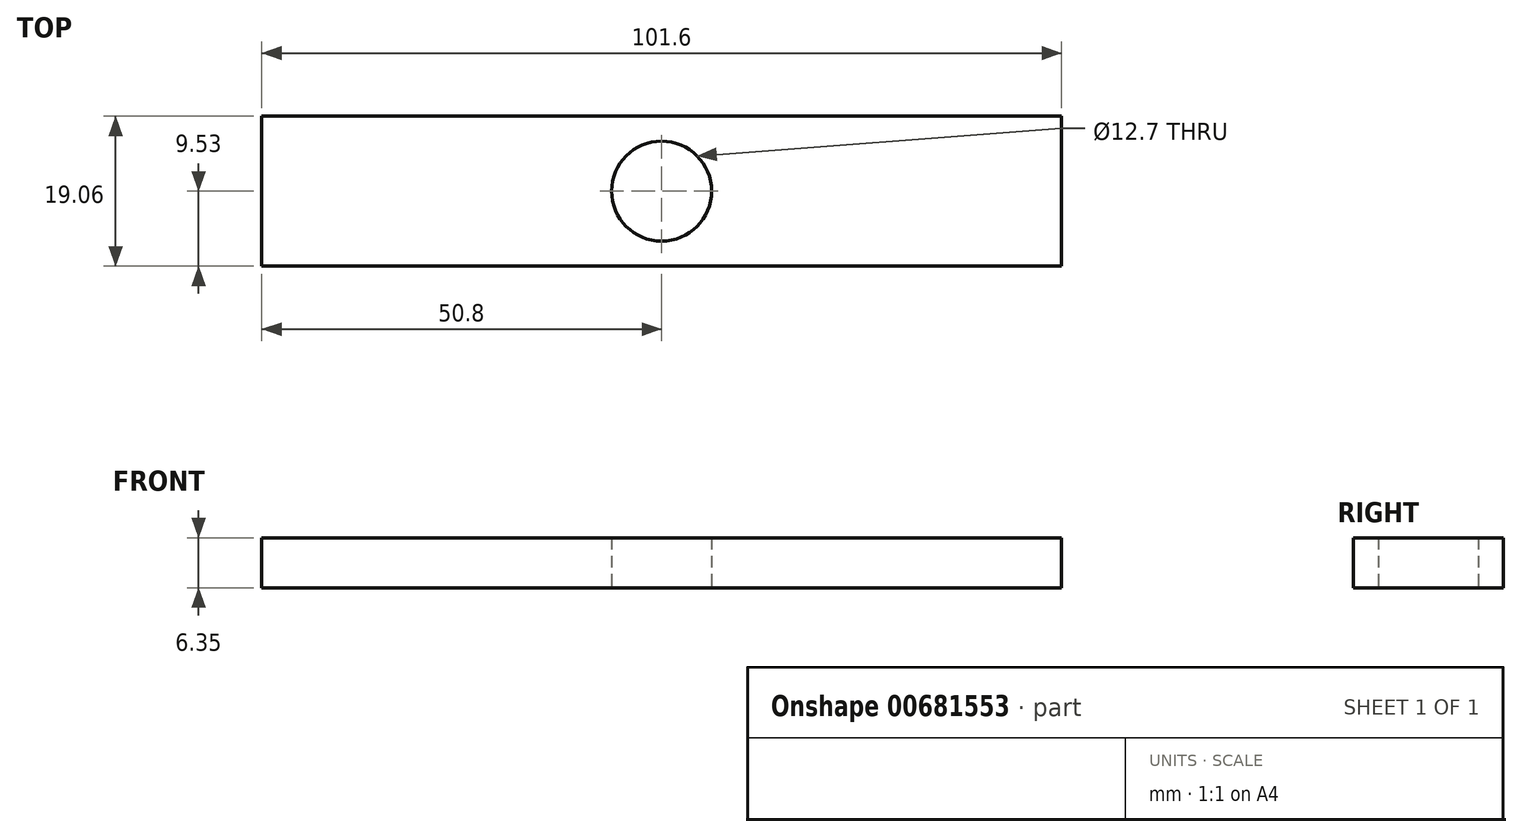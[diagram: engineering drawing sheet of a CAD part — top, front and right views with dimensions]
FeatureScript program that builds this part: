
annotation { "Feature Type Name" : "Feature", "Feature Type Description" : "" }
export const myFeature = defineFeature(function(context is Context, id is Id, definition is map)
    precondition{}
    {
        {
            var Q0;
            Q0=qCreatedBy(makeId("Top.planeOp"),FACE);
            var sketch = newSketch(context, id + "F0", { "sketchPlane" : qUnion([Q0])});
            skLineSegment(sketch, "E0.bottom", {"start": v(50.8, 9.52) * mm, "end": v(-50.8, 9.53) * mm});
            skLineSegment(sketch, "E0.top", {"start": v(50.8, -9.53) * mm, "end": v(-50.8, -9.52) * mm});
            skLineSegment(sketch, "E0.left", {"start": v(50.8, 9.53) * mm, "end": v(50.8, -9.53) * mm});
            skLineSegment(sketch, "E0.right", {"start": v(-50.8, 9.52) * mm, "end": v(-50.8, -9.52) * mm});
            skPoint(sketch, "E0.middle", {"position": v(0, 0) * mm});
            skCircle(sketch, "E1", {"center": v(0, 0) * mm, "radius": 6.35 * mm});
            skPoint(sketch, "E1.centerSnap0", {"position": v(-50.8, 0) * mm});
            skSolve(sketch);
        }
        {
            var Q0;
            Q0 = qSketchRegion(id + "F0", true);
            extrude(context, id + "F1", {"entities" : qUnion([Q0]), "depth" : 6.35 * mm, "offsetDistance" : 25.4 * mm});
        }
    });
